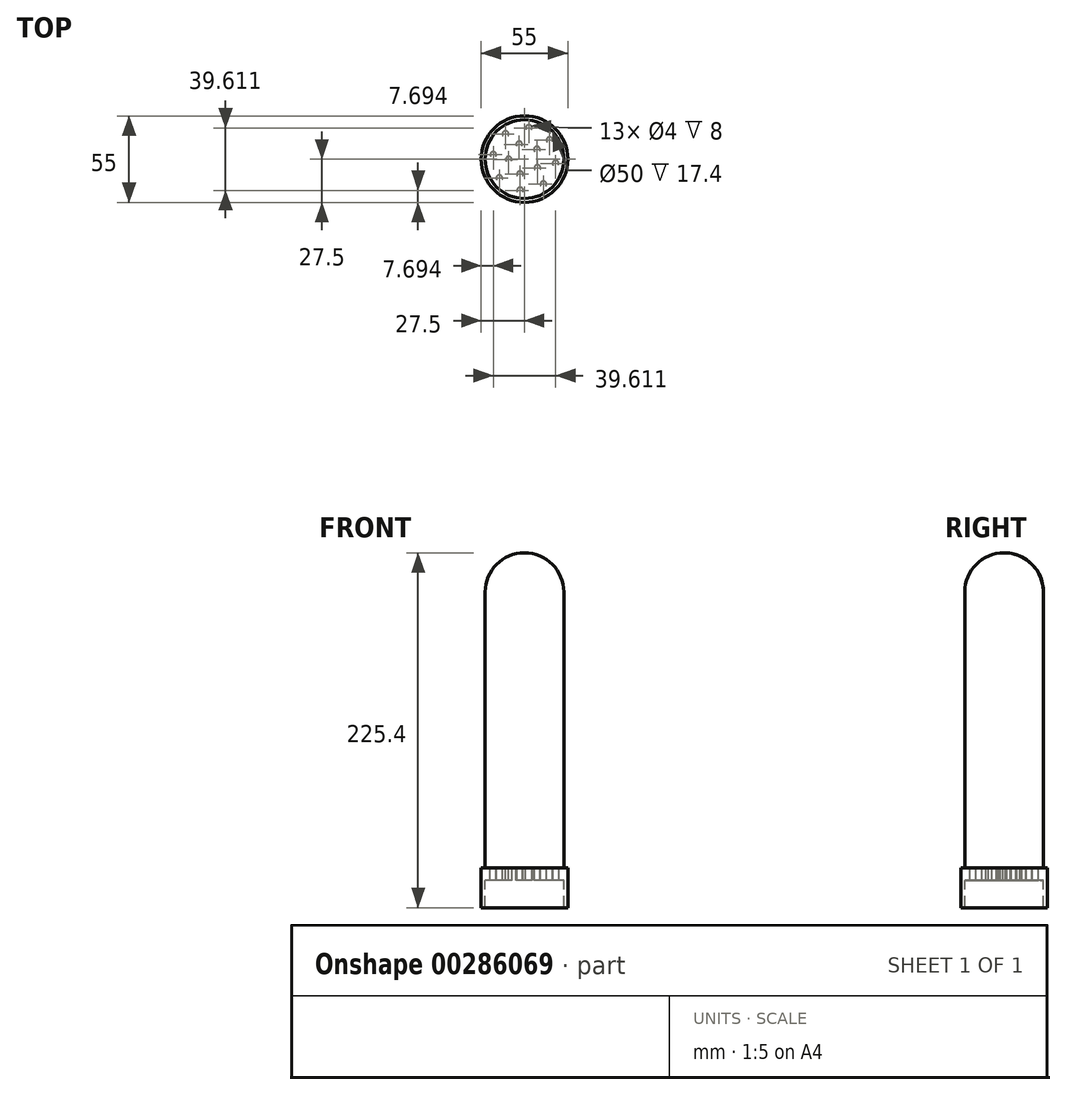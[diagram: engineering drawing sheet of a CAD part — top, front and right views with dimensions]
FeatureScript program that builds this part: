
annotation { "Feature Type Name" : "Feature", "Feature Type Description" : "" }
export const myFeature = defineFeature(function(context is Context, id is Id, definition is map)
    precondition{}
    {
        {
            var Q0;
            Q0=qCreatedBy(makeId("Right.planeOp"),FACE);
            var sketch = newSketch(context, id + "F0", { "sketchPlane" : qUnion([Q0])});
            skLineSegment(sketch, "E0", {"start": v(0, 0) * mm, "end": v(0, 200) * mm});
            skLineSegment(sketch, "E1", {"start": v(0, 0) * mm, "end": v(25, 0) * mm});
            skLineSegment(sketch, "E2", {"start": v(0, 200) * mm, "end": v(0, 175) * mm, "construction": true});
            skArc(sketch, "E3", {"start": v(25, 175) * mm, "mid": v(17.68, 192.68) * mm, "end": v(0, 200) * mm});
            skLineSegment(sketch, "E4", {"start": v(25, 0) * mm, "end": v(25, 175) * mm});
            skSolve(sketch);
        }
        {
            var Q0;
            Q0=makeQuery(id+"F0.imprint","IMPRINT",FACE,{"disambiguationData":[TD([[makeQuery(id+"F0.imprint","IMPRINT",EDGE,{"derivedFrom":sQuery(id+"F0.wireOp",EDGE,"E0")}),-1.0]])]});
            var Q1;
            Q1=sQuery(id+"F0.wireOp",EDGE,"E0");
            revolve(context, id + "F1", {"entities" : qUnion([Q0]), "axis" : qUnion([Q1]), "revolveType" : RevolveType.FULL});
        }
        {
            var Q0;
            Q0=qCreatedBy(makeId("Top.planeOp"),FACE);
            var sketch = newSketch(context, id + "F2", { "sketchPlane" : qUnion([Q0])});
            skCircle(sketch, "E5", {"center": v(0, 0) * mm, "radius": 25 * mm});
            skCircle(sketch, "E6", {"center": v(0, 0) * mm, "radius": 27.5 * mm});
            skSolve(sketch);
        }
        {
            var Q0;
            Q0 = qSketchRegion(id + "F2", true);
            extrude(context, id + "F3", {"entities" : qUnion([Q0]), "oppositeDirection" : true, "depth" : 25.4 * mm});
        }
        {
            var Q0;
            Q0=makeQuery(id+"F2.imprint","IMPRINT",FACE,{"disambiguationData":[TD([[makeQuery(id+"F2.imprint","IMPRINT",EDGE,{"derivedFrom":sQuery(id+"F2.wireOp",EDGE,"E5")}),1.0]])]});
            extrude(context, id + "F4", {"entities" : qUnion([Q0]), "operationType" : NewBodyOperationType.ADD, "oppositeDirection" : true, "depth" : 8 * mm});
        }
        {
            var Q0;
            Q0=makeQuery(id+"F2.imprint","IMPRINT",FACE,{"disambiguationData":[TD([[makeQuery(id+"F2.imprint","IMPRINT",EDGE,{"derivedFrom":sQuery(id+"F2.wireOp",EDGE,"E5")}),-1.0]])]});
            var sketch = newSketch(context, id + "F5", { "sketchPlane" : qUnion([Q0])});
            skLineSegment(sketch, "E7", {"start": v(0, 0) * mm, "end": v(7.91, 6.1) * mm});
            skLineSegment(sketch, "E8", {"start": v(7.91, 6.1) * mm, "end": v(0, 0) * mm});
            skLineSegment(sketch, "E9", {"start": v(0, 0) * mm, "end": v(-19.8, 2.78) * mm});
            skCircle(sketch, "E10", {"center": v(-19.8, 2.78) * mm, "radius": 2 * mm});
            skCircle(sketch, "E11.1.0", {"center": v(-15.97, -12.04) * mm, "radius": 2 * mm});
            skCircle(sketch, "E11.2.0", {"center": v(-2.78, -19.8) * mm, "radius": 2 * mm});
            skCircle(sketch, "E11.3.0", {"center": v(12.04, -15.97) * mm, "radius": 2 * mm});
            skCircle(sketch, "E11.4.0", {"center": v(19.8, -2.78) * mm, "radius": 2 * mm});
            skCircle(sketch, "E11.5.0", {"center": v(15.97, 12.04) * mm, "radius": 2 * mm});
            skCircle(sketch, "E11.6.0", {"center": v(2.78, 19.8) * mm, "radius": 2 * mm});
            skCircle(sketch, "E11.7.0", {"center": v(-12.04, 15.97) * mm, "radius": 2 * mm});
            skPoint(sketch, "E11.center", {"position": v(0, 0) * mm});
            skCircle(sketch, "E12", {"center": v(7.91, 6.1) * mm, "radius": 2 * mm});
            skCircle(sketch, "E13.1.0", {"center": v(-3.35, 9.41) * mm, "radius": 2 * mm});
            skCircle(sketch, "E13.2.0", {"center": v(-9.99, -0.28) * mm, "radius": 2 * mm});
            skCircle(sketch, "E14.1.3.0", {"center": v(-2.82, -9.58) * mm, "radius": 2 * mm});
            skCircle(sketch, "E14.1.4.0", {"center": v(8.24, -5.64) * mm, "radius": 2 * mm});
            skSolve(sketch);
        }
        {
            var Q0;
            Q0 = qSketchRegion(id + "F5", true);
            extrude(context, id + "F6", {"entities" : qUnion([Q0]), "operationType" : NewBodyOperationType.REMOVE, "oppositeDirection" : true, "depth" : 25 * mm});
        }
    });
